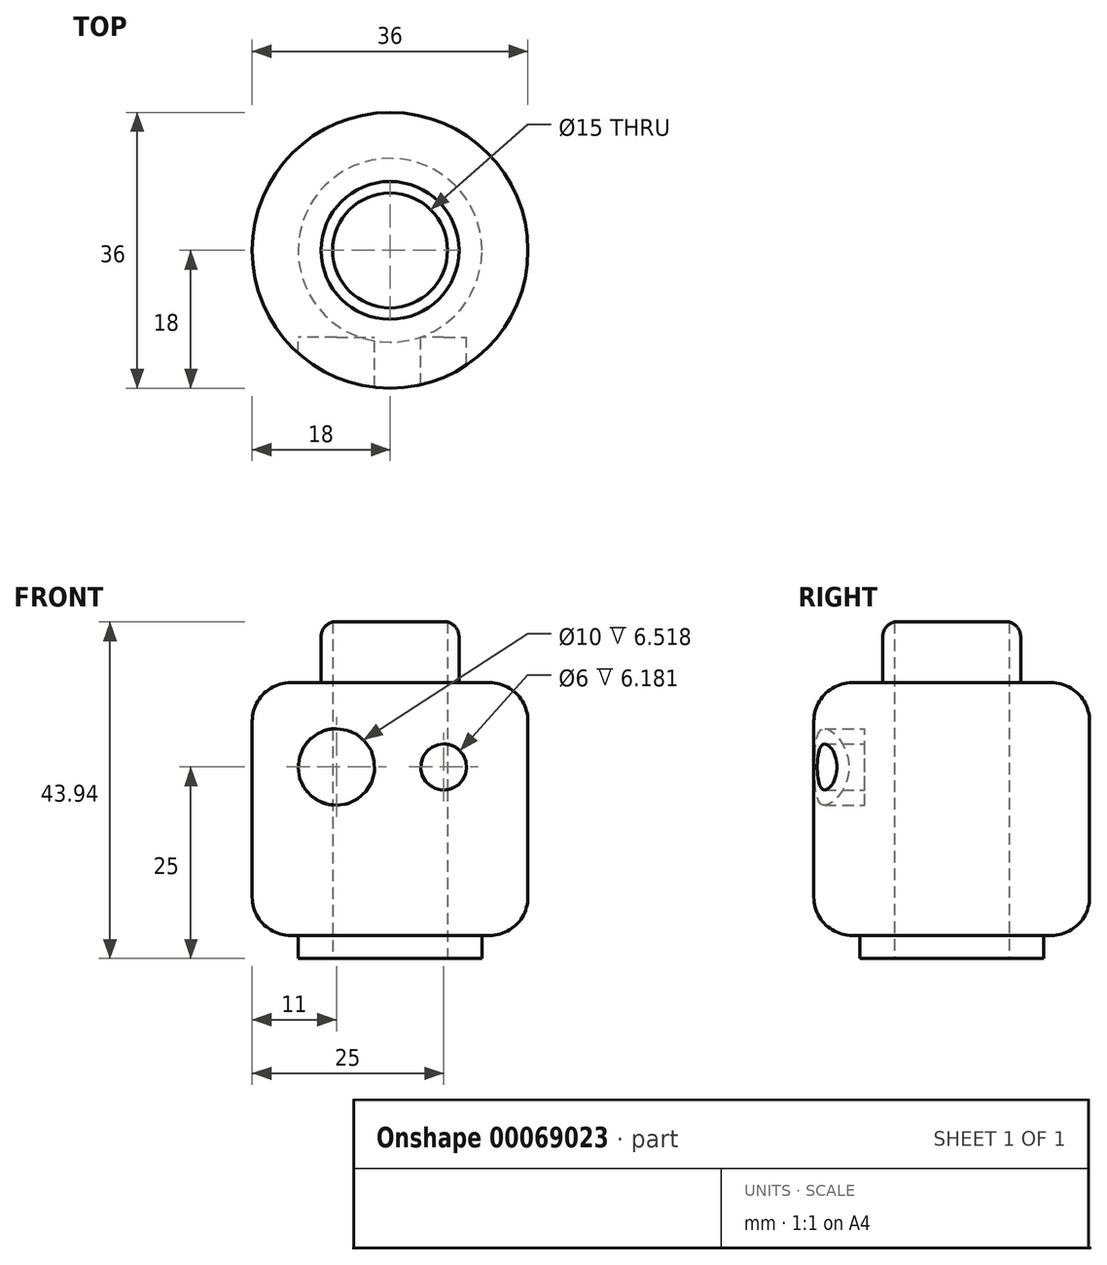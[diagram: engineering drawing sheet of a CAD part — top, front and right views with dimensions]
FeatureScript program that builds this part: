
annotation { "Feature Type Name" : "Feature", "Feature Type Description" : "" }
export const myFeature = defineFeature(function(context is Context, id is Id, definition is map)
    precondition{}
    {
        {
            var Q0;
            Q0=qCreatedBy(makeId("Front.planeOp"),FACE);
            var sketch = newSketch(context, id + "F0", { "sketchPlane" : qUnion([Q0])});
            skLineSegment(sketch, "E0", {"start": v(0, 44) * mm, "end": v(7, 44) * mm});
            skLineSegment(sketch, "E1", {"start": v(9, 42) * mm, "end": v(9, 36) * mm});
            skLineSegment(sketch, "E2", {"start": v(9, 36) * mm, "end": v(13, 36) * mm});
            skLineSegment(sketch, "E3", {"start": v(18, 31) * mm, "end": v(18, 8) * mm});
            skLineSegment(sketch, "E4", {"start": v(13, 3) * mm, "end": v(12, 3) * mm});
            skLineSegment(sketch, "E5", {"start": v(12, 3) * mm, "end": v(12, 0) * mm});
            skLineSegment(sketch, "E6", {"start": v(12, 0) * mm, "end": v(0, 0) * mm});
            skLineSegment(sketch, "E7", {"start": v(0, 0) * mm, "end": v(0, 44) * mm});
            skPoint(sketch, "E8.visualSharp", {"position": v(9, 44) * mm});
            skArc(sketch, "E8.filletArc", {"start": v(9, 42) * mm, "mid": v(8.41, 43.41) * mm, "end": v(7, 44) * mm});
            skPoint(sketch, "E9.visualSharp", {"position": v(18, 36) * mm});
            skArc(sketch, "E9.filletArc", {"start": v(18, 31) * mm, "mid": v(16.54, 34.54) * mm, "end": v(13, 36) * mm});
            skPoint(sketch, "E10.visualSharp", {"position": v(18, 3) * mm});
            skArc(sketch, "E10.filletArc", {"start": v(13, 3) * mm, "mid": v(16.54, 4.46) * mm, "end": v(18, 8) * mm});
            skSolve(sketch);
        }
        {
            var Q0;
            Q0=makeQuery(id+"F0.imprint","IMPRINT",FACE,{"disambiguationData":[TD([[makeQuery(id+"F0.imprint","IMPRINT",EDGE,{"derivedFrom":sQuery(id+"F0.wireOp",EDGE,"E0")}),-1.0]])]});
            var Q1;
            Q1=sQuery(id+"F0.wireOp",EDGE,"E7");
            revolve(context, id + "F1", {"entities" : qUnion([Q0]), "axis" : qUnion([Q1]), "revolveType" : RevolveType.FULL});
        }
        {
            var Q0;
            Q0=makeQuery(id+"F1.opRevolve","SWEPT_FACE",FACE,{"disambiguationData":[OSD([sQuery(id+"F0.wireOp",EDGE,"E6")])]});
            var sketch = newSketch(context, id + "F2", { "sketchPlane" : qUnion([Q0])});
            skCircle(sketch, "E11", {"center": v(0, 0) * mm, "radius": 7.5 * mm});
            skSolve(sketch);
        }
        {
            var Q0;
            Q0=makeQuery(id+"F2.imprint","IMPRINT",FACE,{"disambiguationData":[TD([[makeQuery(id+"F2.imprint","IMPRINT",EDGE,{"derivedFrom":sQuery(id+"F2.wireOp",EDGE,"E11")}),1.0]])]});
            var Q1;
            Q1=makeQuery(id+"F1.opRevolve","SWEPT_FACE",FACE,{"disambiguationData":[OSD([sQuery(id+"F0.wireOp",EDGE,"E0")])]});
            extrude(context, id + "F3", {"entities" : qUnion([Q0]), "operationType" : NewBodyOperationType.REMOVE, "endBound" : BoundingType.UP_TO_SURFACE, "oppositeDirection" : true, "endBoundEntityFace" : qUnion([Q1]), "depth" : 25 * mm});
        }
        {
            var Q0;
            Q0=qCreatedBy(makeId("Front.planeOp"),FACE);
            var sketch = newSketch(context, id + "F4", { "sketchPlane" : qUnion([Q0])});
            skCircle(sketch, "E12", {"center": v(7, 25) * mm, "radius": 3 * mm});
            skCircle(sketch, "E13", {"center": v(-7, 25) * mm, "radius": 5 * mm});
            skSolve(sketch);
        }
        {
            var Q0;
            Q0 = qSketchRegion(id + "F4", true);
            extrude(context, id + "F5", {"entities" : qUnion([Q0]), "operationType" : NewBodyOperationType.REMOVE, "depth" : 20.37 * mm, "hasSecondDirection" : true, "secondDirectionOppositeDirection" : false, "secondDirectionDepth" : 11.37 * mm});
        }
    });
